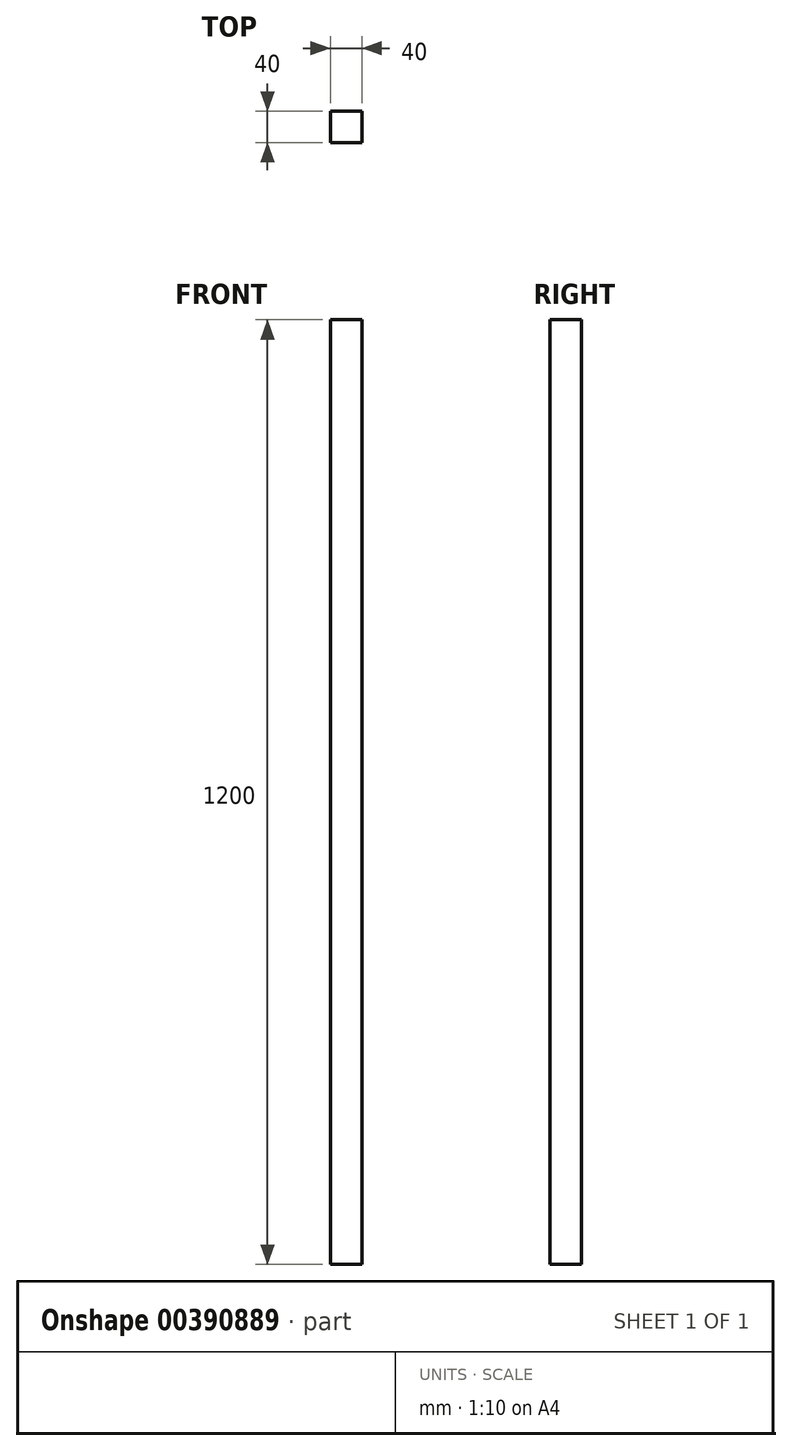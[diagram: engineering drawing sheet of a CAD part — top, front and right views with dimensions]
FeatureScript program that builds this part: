
annotation { "Feature Type Name" : "Feature", "Feature Type Description" : "" }
export const myFeature = defineFeature(function(context is Context, id is Id, definition is map)
    precondition{}
    {
        {
            var Q0;
            Q0=qCreatedBy(makeId("Top.planeOp"),FACE);
            var sketch = newSketch(context, id + "F0", { "sketchPlane" : qUnion([Q0])});
            skLineSegment(sketch, "E0.bottom", {"start": v(-19.8, 21.05) * mm, "end": v(20.2, 21.05) * mm});
            skLineSegment(sketch, "E0.top", {"start": v(-19.8, -18.95) * mm, "end": v(20.2, -18.95) * mm});
            skLineSegment(sketch, "E0.left", {"start": v(-19.8, 21.05) * mm, "end": v(-19.8, -18.95) * mm});
            skLineSegment(sketch, "E0.right", {"start": v(20.2, 21.05) * mm, "end": v(20.2, -18.95) * mm});
            skSolve(sketch);
        }
        {
            var Q0;
            Q0 = qSketchRegion(id + "F0", true);
            extrude(context, id + "F1", {"entities" : qUnion([Q0]), "depth" : 1200 * mm});
        }
    });
